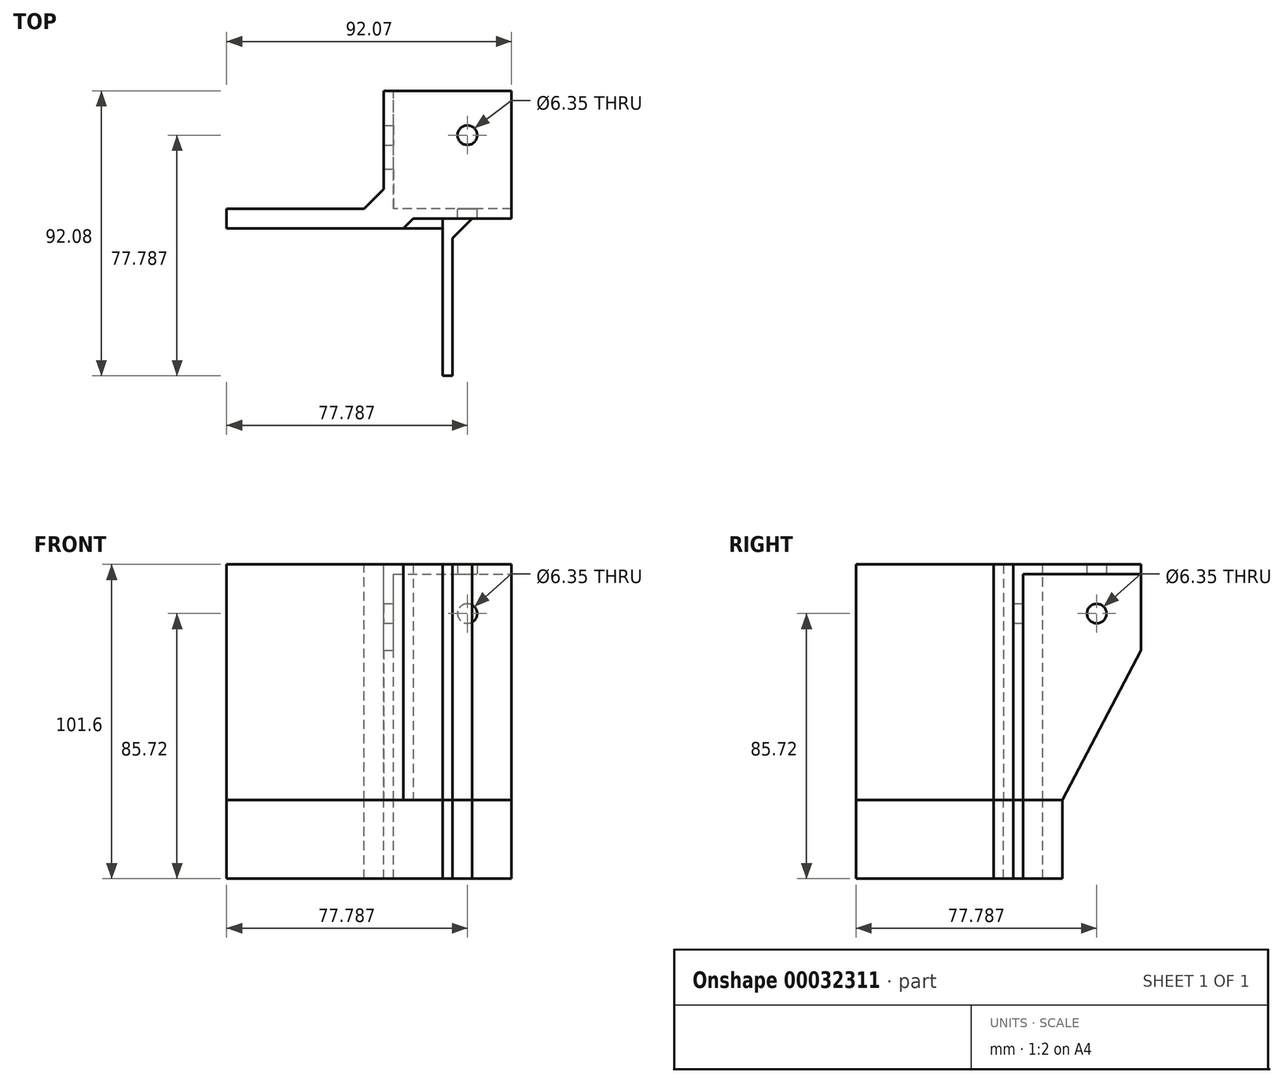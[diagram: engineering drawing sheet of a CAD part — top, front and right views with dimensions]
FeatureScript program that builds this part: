
annotation { "Feature Type Name" : "Feature", "Feature Type Description" : "" }
export const myFeature = defineFeature(function(context is Context, id is Id, definition is map)
    precondition{}
    {
        {
            var Q0;
            Q0=qCreatedBy(makeId("Top.planeOp"),FACE);
            var sketch = newSketch(context, id + "F0", { "sketchPlane" : qUnion([Q0])});
            skLineSegment(sketch, "E0.bottom", {"start": v(0, 0) * mm, "end": v(50.8, 0) * mm});
            skLineSegment(sketch, "E0.top", {"start": v(0, 50.8) * mm, "end": v(50.8, 50.8) * mm});
            skLineSegment(sketch, "E0.left", {"start": v(0, 0) * mm, "end": v(0, 50.8) * mm});
            skLineSegment(sketch, "E0.right", {"start": v(50.8, 0) * mm, "end": v(50.8, 50.8) * mm});
            skSolve(sketch);
        }
        {
            var Q0;
            Q0=makeQuery(id+"F0.imprint","IMPRINT",FACE,{"disambiguationData":[TD([[makeQuery(id+"F0.imprint","IMPRINT",EDGE,{"derivedFrom":sQuery(id+"F0.wireOp",EDGE,"E0.bottom")}),1.0]])]});
            extrude(context, id + "F1", {"entities" : qUnion([Q0]), "depth" : 3.17 * mm});
        }
        {
            var Q0;
            Q0=makeQuery(id+"F1.opExtrude","CAP_FACE",FACE,{"disambiguationData":[OSD([sQuery(id+"F0.wireOp",EDGE,"E0.bottom"),sQuery(id+"F0.wireOp",EDGE,"E0.top"),sQuery(id+"F0.wireOp",EDGE,"E0.left"),sQuery(id+"F0.wireOp",EDGE,"E0.right")])],"isStart":false});
            var sketch = newSketch(context, id + "F2", { "sketchPlane" : qUnion([Q0])});
            skLineSegment(sketch, "E1.bottom", {"start": v(50.8, 0) * mm, "end": v(-50.8, 0) * mm});
            skLineSegment(sketch, "E1.top", {"start": v(50.8, 3.18) * mm, "end": v(-50.8, 3.18) * mm});
            skLineSegment(sketch, "E1.left", {"start": v(50.8, 0) * mm, "end": v(50.8, 3.18) * mm});
            skLineSegment(sketch, "E1.right", {"start": v(-50.8, 0) * mm, "end": v(-50.8, 3.18) * mm});
            skSolve(sketch);
        }
        {
            var Q0;
            {var subQ5=sQuery(id+"F2.wireOp",EDGE,"E1.right");Q0=makeQuery(id+"F2.imprint","IMPRINT",FACE,{"disambiguationData":[TD([[makeQuery(id+"F2.imprint","IMPRINT",EDGE,{"derivedFrom":subQ5}),-1.0]])]});}
            var Q1;
            {var subQ5=sQuery(id+"F2.wireOp",EDGE,"E1.left");Q1=makeQuery(id+"F2.imprint","IMPRINT",FACE,{"disambiguationData":[TD([[makeQuery(id+"F2.imprint","IMPRINT",EDGE,{"derivedFrom":subQ5}),1.0]])]});}
            extrude(context, id + "F3", {"entities" : qUnion([Q0, Q1]), "operationType" : NewBodyOperationType.ADD, "depth" : 12.7 * mm, "hasSecondDirection" : true, "secondDirectionOppositeDirection" : true, "secondDirectionDepth" : 76.2 * mm});
        }
        {
            var Q0;
            Q0=makeQuery(id+"F1.opExtrude","CAP_FACE",FACE,{"disambiguationData":[OSD([sQuery(id+"F0.wireOp",EDGE,"E0.bottom"),sQuery(id+"F0.wireOp",EDGE,"E0.top"),sQuery(id+"F0.wireOp",EDGE,"E0.left"),sQuery(id+"F0.wireOp",EDGE,"E0.right")])],"isStart":false});
            var sketch = newSketch(context, id + "F4", { "sketchPlane" : qUnion([Q0])});
            skLineSegment(sketch, "E2.bottom", {"start": v(0, 50.8) * mm, "end": v(3.18, 50.8) * mm});
            skLineSegment(sketch, "E2.top", {"start": v(0, -50.8) * mm, "end": v(3.18, -50.8) * mm});
            skLineSegment(sketch, "E2.left", {"start": v(0, 50.8) * mm, "end": v(0, -50.8) * mm});
            skLineSegment(sketch, "E2.right", {"start": v(3.18, 50.8) * mm, "end": v(3.18, -50.8) * mm});
            skSolve(sketch);
        }
        {
            var Q0;
            Q0=qSketchRegion(id+"F4",true);
            extrude(context, id + "F5", {"entities" : qUnion([Q0]), "operationType" : NewBodyOperationType.ADD, "depth" : 12.7 * mm, "hasSecondDirection" : true, "secondDirectionOppositeDirection" : true, "secondDirectionDepth" : 76.2 * mm});
        }
        {
            var Q0;
            Q0=makeQuery(id+"F5.boolean.opBoolean","MERGE",FACE,{"derivedFrom":[makeQuery(id+"F3.opExtrude","CAP_FACE",FACE,{"disambiguationData":[OSD([sQuery(id+"F2.wireOp",EDGE,"E1.bottom"),sQuery(id+"F2.wireOp",EDGE,"E1.top"),sQuery(id+"F2.wireOp",EDGE,"E1.left"),sQuery(id+"F2.wireOp",EDGE,"E1.right")])],"isStart":false}),makeQuery(id+"F5.opExtrude","CAP_FACE",FACE,{"disambiguationData":[OSD([sQuery(id+"F4.wireOp",EDGE,"E2.bottom"),sQuery(id+"F4.wireOp",EDGE,"E2.top"),sQuery(id+"F4.wireOp",EDGE,"E2.left"),sQuery(id+"F4.wireOp",EDGE,"E2.right")])],"isStart":false})]});
            var sketch = newSketch(context, id + "F6", { "sketchPlane" : qUnion([Q0])});
            skLineSegment(sketch, "E3.0", {"start": v(3.18, 50.8) * mm, "end": v(3.18, 3.18) * mm});
            skLineSegment(sketch, "E3.1", {"start": v(0, 50.8) * mm, "end": v(3.18, 50.8) * mm});
            skLineSegment(sketch, "E3.2", {"start": v(0, 50.8) * mm, "end": v(0, 3.18) * mm});
            skLineSegment(sketch, "E3.3", {"start": v(50.8, 3.18) * mm, "end": v(3.18, 3.18) * mm});
            skLineSegment(sketch, "E3.4", {"start": v(50.8, 0) * mm, "end": v(3.18, 0) * mm});
            skLineSegment(sketch, "E3.5", {"start": v(50.8, 0) * mm, "end": v(50.8, 3.18) * mm});
            skLineSegment(sketch, "E4", {"start": v(3.18, 0) * mm, "end": v(0, 0) * mm});
            skLineSegment(sketch, "E5", {"start": v(0, 0) * mm, "end": v(0, 3.18) * mm});
            skSolve(sketch);
        }
        {
            var Q0;
            {var subQ0=sQuery(id+"F4.wireOp",EDGE,"E2.right");var subQ3=sQuery(id+"F0.wireOp",EDGE,"E0.top");Q0=makeQuery(id+"F5.boolean.opBoolean","SPLIT",FACE,{"disambiguationData":[TD([makeQuery(id+"F1.opExtrude","CAP_FACE",FACE,{"disambiguationData":[OSD([sQuery(id+"F0.wireOp",EDGE,"E0.bottom"),subQ3,sQuery(id+"F0.wireOp",EDGE,"E0.left"),sQuery(id+"F0.wireOp",EDGE,"E0.right")])],"isStart":false})])],"derivedFrom":makeQuery(id+"F5.opExtrude","SWEPT_FACE",FACE,{"disambiguationData":[OSD([subQ0])]})});}
            var sketch = newSketch(context, id + "F7", { "sketchPlane" : qUnion([Q0])});
            skLineSegment(sketch, "E6.0", {"start": v(50.8, 15.88) * mm, "end": v(50.8, 3.18) * mm});
            skLineSegment(sketch, "E6.1", {"start": v(3.18, 3.18) * mm, "end": v(50.8, 3.18) * mm});
            skLineSegment(sketch, "E6.2", {"start": v(50.8, 15.88) * mm, "end": v(3.18, 15.88) * mm});
            skLineSegment(sketch, "E6.3", {"start": v(3.18, 3.18) * mm, "end": v(3.18, 15.88) * mm});
            skSolve(sketch);
        }
        {
            var Q0;
            Q0=makeQuery(id+"F7.imprint","IMPRINT",FACE,{"disambiguationData":[TD([[makeQuery(id+"F7.imprint","IMPRINT",EDGE,{"derivedFrom":sQuery(id+"F7.wireOp",EDGE,"E6.0")}),-1.0]])]});
            extrude(context, id + "F8", {"entities" : qUnion([Q0]), "operationType" : NewBodyOperationType.REMOVE, "oppositeDirection" : true, "depth" : 25.4 * mm});
        }
        {
            var Q0;
            {var subQ0=sQuery(id+"F2.wireOp",EDGE,"E1.top");var subQ1=makeQuery(id+"F3.opExtrude","SWEPT_FACE",FACE,{"disambiguationData":[OSD([subQ0])]});var subQ11=sQuery(id+"F0.wireOp",EDGE,"E0.left");var subQ12=sQuery(id+"F0.wireOp",EDGE,"E0.right");Q0=makeQuery(id+"F8.boolean.opBoolean","MERGE",FACE,{"derivedFrom":[makeQuery(id+"F5.boolean.opBoolean","SPLIT",FACE,{"disambiguationData":[TD([makeQuery(id+"F1.opExtrude","SWEPT_FACE",FACE,{"disambiguationData":[OSD([subQ11])]})])],"derivedFrom":subQ1}),makeQuery(id+"F5.boolean.opBoolean","SPLIT",FACE,{"disambiguationData":[TD([makeQuery(id+"F1.opExtrude","CAP_FACE",FACE,{"disambiguationData":[OSD([sQuery(id+"F0.wireOp",EDGE,"E0.bottom"),sQuery(id+"F0.wireOp",EDGE,"E0.top"),subQ11,subQ12])],"isStart":false})])],"derivedFrom":subQ1}),makeQuery(id+"F8.opExtrude","SWEPT_FACE",FACE,{"disambiguationData":[OSD([sQuery(id+"F7.wireOp",EDGE,"E6.3")])]})]});}
            var sketch = newSketch(context, id + "F9", { "sketchPlane" : qUnion([Q0])});
            skLineSegment(sketch, "E7.0", {"start": v(-50.8, 15.88) * mm, "end": v(-3.18, 15.88) * mm});
            skLineSegment(sketch, "E7.1", {"start": v(-3.18, 3.18) * mm, "end": v(-50.8, 3.18) * mm});
            skLineSegment(sketch, "E7.2", {"start": v(-50.8, 15.88) * mm, "end": v(-50.8, 3.18) * mm});
            skLineSegment(sketch, "E8", {"start": v(-3.18, 15.88) * mm, "end": v(-3.18, 3.18) * mm});
            skPoint(sketch, "E9.orphan", {"position": v(0, 3.18) * mm});
            skSolve(sketch);
        }
        {
            var Q0;
            Q0=makeQuery(id+"F9.imprint","IMPRINT",FACE,{"disambiguationData":[TD([[makeQuery(id+"F9.imprint","IMPRINT",EDGE,{"derivedFrom":sQuery(id+"F9.wireOp",EDGE,"E7.0")}),-1.0]])]});
            extrude(context, id + "F10", {"entities" : qUnion([Q0]), "operationType" : NewBodyOperationType.REMOVE, "oppositeDirection" : true, "depth" : 25.4 * mm});
        }
        {
            var Q0;
            {var subQ0=sQuery(id+"F2.wireOp",EDGE,"E1.bottom");Q0=makeQuery(id+"F5.boolean.opBoolean","SPLIT",FACE,{"disambiguationData":[TD([makeQuery(id+"F1.opExtrude","SWEPT_FACE",FACE,{"disambiguationData":[OSD([sQuery(id+"F0.wireOp",EDGE,"E0.right")])]})])],"derivedFrom":makeQuery(id+"F3.boolean.opBoolean","MERGE",FACE,{"derivedFrom":[makeQuery(id+"F1.opExtrude","SWEPT_FACE",FACE,{"disambiguationData":[OSD([sQuery(id+"F0.wireOp",EDGE,"E0.bottom")])]}),makeQuery(id+"F3.opExtrude","SWEPT_FACE",FACE,{"disambiguationData":[OSD([subQ0])]})]})});}
            var sketch = newSketch(context, id + "F11", { "sketchPlane" : qUnion([Q0])});
            skLineSegment(sketch, "E10", {"start": v(3.18, -73.03) * mm, "end": v(41.28, -73.03) * mm, "construction": true});
            skLineSegment(sketch, "E11", {"start": v(50.8, 0) * mm, "end": v(50.8, -6.35) * mm, "construction": true});
            skLineSegment(sketch, "E12", {"start": v(41.28, -73.03) * mm, "end": v(50.8, -6.35) * mm});
            skLineSegment(sketch, "E13", {"start": v(50.8, -6.35) * mm, "end": v(50.8, -73.03) * mm});
            skLineSegment(sketch, "E14", {"start": v(50.8, -73.03) * mm, "end": v(41.28, -73.03) * mm});
            skSolve(sketch);
        }
        {
            var Q0;
            Q0=makeQuery(id+"F11.imprint","IMPRINT",FACE,{"disambiguationData":[TD([[makeQuery(id+"F11.imprint","IMPRINT",EDGE,{"derivedFrom":sQuery(id+"F11.wireOp",EDGE,"E12")}),-1.0]])]});
            extrude(context, id + "F12", {"entities" : qUnion([Q0]), "operationType" : NewBodyOperationType.REMOVE, "oppositeDirection" : true, "depth" : 25.4 * mm});
        }
        {
            var Q0;
            Q0=makeQuery(id+"F5.boolean.opBoolean","MERGE",FACE,{"derivedFrom":[makeQuery(id+"F1.opExtrude","SWEPT_FACE",FACE,{"disambiguationData":[OSD([sQuery(id+"F0.wireOp",EDGE,"E0.left")])]}),makeQuery(id+"F5.opExtrude","SWEPT_FACE",FACE,{"disambiguationData":[OSD([sQuery(id+"F4.wireOp",EDGE,"E2.left")])]})]});
            var sketch = newSketch(context, id + "F13", { "sketchPlane" : qUnion([Q0])});
            skLineSegment(sketch, "E15", {"start": v(-50.8, 3.18) * mm, "end": v(-50.8, -6.35) * mm, "construction": true});
            skLineSegment(sketch, "E16", {"start": v(-50.8, -6.35) * mm, "end": v(-15.88, -73.03) * mm});
            skLineSegment(sketch, "E17", {"start": v(-15.88, -73.03) * mm, "end": v(-3.18, -73.03) * mm, "construction": true});
            skLineSegment(sketch, "E18", {"start": v(-50.8, -6.35) * mm, "end": v(-50.8, -73.03) * mm});
            skLineSegment(sketch, "E19", {"start": v(-50.8, -73.03) * mm, "end": v(-15.88, -73.03) * mm});
            skSolve(sketch);
        }
        {
            var Q0;
            Q0=makeQuery(id+"F13.imprint","IMPRINT",FACE,{"disambiguationData":[TD([[makeQuery(id+"F13.imprint","IMPRINT",EDGE,{"derivedFrom":sQuery(id+"F13.wireOp",EDGE,"E16")}),-1.0]])]});
            extrude(context, id + "F14", {"entities" : qUnion([Q0]), "operationType" : NewBodyOperationType.REMOVE, "oppositeDirection" : true, "depth" : 25.4 * mm});
        }
        {
            var Q0;
            {var subQ0=sQuery(id+"F2.wireOp",EDGE,"E1.top");var subQ1=makeQuery(id+"F3.opExtrude","SWEPT_FACE",FACE,{"disambiguationData":[OSD([subQ0])]});var subQ11=sQuery(id+"F0.wireOp",EDGE,"E0.left");var subQ12=sQuery(id+"F0.wireOp",EDGE,"E0.right");Q0=makeQuery(id+"F8.boolean.opBoolean","MERGE",FACE,{"derivedFrom":[makeQuery(id+"F5.boolean.opBoolean","SPLIT",FACE,{"disambiguationData":[TD([makeQuery(id+"F1.opExtrude","SWEPT_FACE",FACE,{"disambiguationData":[OSD([subQ11])]})])],"derivedFrom":subQ1}),makeQuery(id+"F5.boolean.opBoolean","SPLIT",FACE,{"disambiguationData":[TD([makeQuery(id+"F1.opExtrude","CAP_FACE",FACE,{"disambiguationData":[OSD([sQuery(id+"F0.wireOp",EDGE,"E0.bottom"),sQuery(id+"F0.wireOp",EDGE,"E0.top"),subQ11,subQ12])],"isStart":false})])],"derivedFrom":subQ1}),makeQuery(id+"F8.opExtrude","SWEPT_FACE",FACE,{"disambiguationData":[OSD([sQuery(id+"F7.wireOp",EDGE,"E6.3")])]})]});}
            var sketch = newSketch(context, id + "F15", { "sketchPlane" : qUnion([Q0])});
            skLineSegment(sketch, "E20.bottom", {"start": v(-3.18, 15.88) * mm, "end": v(50.8, 15.88) * mm});
            skLineSegment(sketch, "E20.top", {"start": v(-3.18, 3.18) * mm, "end": v(50.8, 3.18) * mm});
            skLineSegment(sketch, "E20.left", {"start": v(-3.18, 15.88) * mm, "end": v(-3.18, 3.18) * mm});
            skLineSegment(sketch, "E20.right", {"start": v(50.8, 15.88) * mm, "end": v(50.8, 3.18) * mm});
            skSolve(sketch);
        }
        {
            var Q0;
            Q0=makeQuery(id+"F15.imprint","IMPRINT",FACE,{"disambiguationData":[TD([[makeQuery(id+"F15.imprint","IMPRINT",EDGE,{"derivedFrom":sQuery(id+"F15.wireOp",EDGE,"E20.bottom")}),-1.0]])]});
            extrude(context, id + "F16", {"entities" : qUnion([Q0]), "operationType" : NewBodyOperationType.REMOVE, "endBound" : BoundingType.THROUGH_ALL, "oppositeDirection" : true, "depth" : 25.4 * mm});
        }
        {
            var Q0;
            Q0=makeQuery(id+"F16.boolean.opBoolean","MERGE",FACE,{"derivedFrom":[makeQuery(id+"F10.boolean.opBoolean","MERGE",FACE,{"derivedFrom":[makeQuery(id+"F8.boolean.opBoolean","MERGE",FACE,{"derivedFrom":[makeQuery(id+"F1.opExtrude","CAP_FACE",FACE,{"disambiguationData":[OSD([sQuery(id+"F0.wireOp",EDGE,"E0.bottom"),sQuery(id+"F0.wireOp",EDGE,"E0.top"),sQuery(id+"F0.wireOp",EDGE,"E0.left"),sQuery(id+"F0.wireOp",EDGE,"E0.right")])],"isStart":false}),makeQuery(id+"F8.opExtrude","SWEPT_FACE",FACE,{"disambiguationData":[OSD([sQuery(id+"F7.wireOp",EDGE,"E6.1")])]})]}),makeQuery(id+"F10.opExtrude","SWEPT_FACE",FACE,{"disambiguationData":[OSD([sQuery(id+"F9.wireOp",EDGE,"E7.1")])]})]}),makeQuery(id+"F16.opExtrude","SWEPT_FACE",FACE,{"disambiguationData":[OSD([sQuery(id+"F15.wireOp",EDGE,"E20.top")])]})]});
            var sketch = newSketch(context, id + "F17", { "sketchPlane" : qUnion([Q0])});
            skLineSegment(sketch, "E21", {"start": v(3.18, 0) * mm, "end": v(3.18, -6.35) * mm});
            skLineSegment(sketch, "E22", {"start": v(3.18, -6.35) * mm, "end": v(9.53, 0) * mm});
            skLineSegment(sketch, "E23", {"start": v(9.53, 0) * mm, "end": v(3.18, 0) * mm});
            skLineSegment(sketch, "E24", {"start": v(0, 3.18) * mm, "end": v(0, 9.53) * mm});
            skLineSegment(sketch, "E25", {"start": v(0, 9.53) * mm, "end": v(-6.35, 3.18) * mm});
            skLineSegment(sketch, "E26", {"start": v(-6.35, 3.18) * mm, "end": v(0, 3.18) * mm});
            skSolve(sketch);
        }
        {
            var Q0;
            Q0=qSketchRegion(id+"F17",true);
            var Q1;
            Q1=makeQuery(id+"F5.boolean.opBoolean","MERGE",FACE,{"derivedFrom":[makeQuery(id+"F3.opExtrude","CAP_FACE",FACE,{"disambiguationData":[OSD([sQuery(id+"F2.wireOp",EDGE,"E1.bottom"),sQuery(id+"F2.wireOp",EDGE,"E1.top"),sQuery(id+"F2.wireOp",EDGE,"E1.left"),sQuery(id+"F2.wireOp",EDGE,"E1.right")])],"isStart":true}),makeQuery(id+"F5.opExtrude","CAP_FACE",FACE,{"disambiguationData":[OSD([sQuery(id+"F4.wireOp",EDGE,"E2.bottom"),sQuery(id+"F4.wireOp",EDGE,"E2.top"),sQuery(id+"F4.wireOp",EDGE,"E2.left"),sQuery(id+"F4.wireOp",EDGE,"E2.right")])],"isStart":true})]});
            extrude(context, id + "F18", {"entities" : qUnion([Q0]), "operationType" : NewBodyOperationType.ADD, "endBound" : BoundingType.UP_TO_SURFACE, "oppositeDirection" : true, "endBoundEntityFace" : qUnion([Q1]), "depth" : 25.4 * mm});
        }
        {
            var Q0;
            {var subQ0=sQuery(id+"F2.wireOp",EDGE,"E1.top");var subQ3=sQuery(id+"F0.wireOp",EDGE,"E0.right");Q0=makeQuery(id+"F5.boolean.opBoolean","SPLIT",FACE,{"disambiguationData":[TD([makeQuery(id+"F1.opExtrude","CAP_FACE",FACE,{"disambiguationData":[OSD([sQuery(id+"F0.wireOp",EDGE,"E0.bottom"),sQuery(id+"F0.wireOp",EDGE,"E0.top"),sQuery(id+"F0.wireOp",EDGE,"E0.left"),subQ3])],"isStart":true})])],"derivedFrom":makeQuery(id+"F3.opExtrude","SWEPT_FACE",FACE,{"disambiguationData":[OSD([subQ0])]})});}
            var sketch = newSketch(context, id + "F19", { "sketchPlane" : qUnion([Q0])});
            skLineSegment(sketch, "E27", {"start": v(-26.99, 0) * mm, "end": v(-26.99, -12.7) * mm, "construction": true});
            skPoint(sketch, "E27.endSnap0", {"position": v(-26.99, 0) * mm});
            skCircle(sketch, "E28", {"center": v(-26.99, -12.7) * mm, "radius": 3.18 * mm});
            skSolve(sketch);
        }
        {
            var Q0;
            Q0=qSketchRegion(id+"F19",true);
            extrude(context, id + "F20", {"entities" : qUnion([Q0]), "operationType" : NewBodyOperationType.REMOVE, "oppositeDirection" : true, "depth" : 25.4 * mm});
        }
        {
            var Q0;
            {var subQ0=sQuery(id+"F4.wireOp",EDGE,"E2.right");var subQ3=sQuery(id+"F0.wireOp",EDGE,"E0.top");Q0=makeQuery(id+"F5.boolean.opBoolean","SPLIT",FACE,{"disambiguationData":[TD([makeQuery(id+"F1.opExtrude","CAP_FACE",FACE,{"disambiguationData":[OSD([sQuery(id+"F0.wireOp",EDGE,"E0.bottom"),subQ3,sQuery(id+"F0.wireOp",EDGE,"E0.left"),sQuery(id+"F0.wireOp",EDGE,"E0.right")])],"isStart":true})])],"derivedFrom":makeQuery(id+"F5.opExtrude","SWEPT_FACE",FACE,{"disambiguationData":[OSD([subQ0])]})});}
            var sketch = newSketch(context, id + "F21", { "sketchPlane" : qUnion([Q0])});
            skLineSegment(sketch, "E29", {"start": v(26.99, 0) * mm, "end": v(26.99, -12.7) * mm, "construction": true});
            skPoint(sketch, "E29.endSnap0", {"position": v(26.99, 0) * mm});
            skCircle(sketch, "E30", {"center": v(26.99, -12.7) * mm, "radius": 3.18 * mm});
            skSolve(sketch);
        }
        {
            var Q0;
            Q0=makeQuery(id+"F21.imprint","IMPRINT",FACE,{"disambiguationData":[TD([[makeQuery(id+"F21.imprint","IMPRINT",EDGE,{"derivedFrom":sQuery(id+"F21.wireOp",EDGE,"E30")}),1.0]])]});
            extrude(context, id + "F22", {"entities" : qUnion([Q0]), "operationType" : NewBodyOperationType.REMOVE, "oppositeDirection" : true, "depth" : 25.4 * mm});
        }
        {
            var Q0;
            Q0=makeQuery(id+"F1.opExtrude","CAP_FACE",FACE,{"disambiguationData":[OSD([sQuery(id+"F0.wireOp",EDGE,"E0.bottom"),sQuery(id+"F0.wireOp",EDGE,"E0.top"),sQuery(id+"F0.wireOp",EDGE,"E0.left"),sQuery(id+"F0.wireOp",EDGE,"E0.right")])],"isStart":true});
            var sketch = newSketch(context, id + "F23", { "sketchPlane" : qUnion([Q0])});
            skLineSegment(sketch, "E31", {"start": v(3.18, -3.18) * mm, "end": v(50.8, -50.8) * mm, "construction": true});
            skLineSegment(sketch, "E32", {"start": v(50.8, -50.8) * mm, "end": v(50.8, -3.18) * mm, "construction": true});
            skLineSegment(sketch, "E33", {"start": v(50.8, -3.18) * mm, "end": v(3.17, -50.8) * mm, "construction": true});
            skCircle(sketch, "E34", {"center": v(26.99, -26.99) * mm, "radius": 3.18 * mm});
            skPoint(sketch, "E34.centerSnap0", {"position": v(26.99, -26.99) * mm});
            skSolve(sketch);
        }
        {
            var Q0;
            Q0=makeQuery(id+"F23.imprint","IMPRINT",FACE,{"disambiguationData":[TD([[makeQuery(id+"F23.imprint","IMPRINT",EDGE,{"derivedFrom":sQuery(id+"F23.wireOp",EDGE,"E34")}),1.0]])]});
            var Q1;
            Q1=sQuery(id+"F23.wireOp",EDGE,"E34");
            extrude(context, id + "F24", {"entities" : qUnion([Q0]), "operationType" : NewBodyOperationType.REMOVE, "surfaceEntities" : qUnion([Q1]), "oppositeDirection" : true, "depth" : 25.4 * mm});
        }
        {
            var Q0;
            Q0=makeQuery(id+"F18.boolean.opBoolean","MERGE",FACE,{"derivedFrom":[makeQuery(id+"F16.boolean.opBoolean","MERGE",FACE,{"derivedFrom":[makeQuery(id+"F10.boolean.opBoolean","MERGE",FACE,{"derivedFrom":[makeQuery(id+"F8.boolean.opBoolean","MERGE",FACE,{"derivedFrom":[makeQuery(id+"F1.opExtrude","CAP_FACE",FACE,{"disambiguationData":[OSD([sQuery(id+"F0.wireOp",EDGE,"E0.bottom"),sQuery(id+"F0.wireOp",EDGE,"E0.top"),sQuery(id+"F0.wireOp",EDGE,"E0.left"),sQuery(id+"F0.wireOp",EDGE,"E0.right")])],"isStart":false}),makeQuery(id+"F8.opExtrude","SWEPT_FACE",FACE,{"disambiguationData":[OSD([sQuery(id+"F7.wireOp",EDGE,"E6.1")])]})]}),makeQuery(id+"F10.opExtrude","SWEPT_FACE",FACE,{"disambiguationData":[OSD([sQuery(id+"F9.wireOp",EDGE,"E7.1")])]})]}),makeQuery(id+"F16.opExtrude","SWEPT_FACE",FACE,{"disambiguationData":[OSD([sQuery(id+"F15.wireOp",EDGE,"E20.top")])]})]}),makeQuery(id+"F18.opExtrude","CAP_FACE",FACE,{"disambiguationData":[OSD([sQuery(id+"F17.wireOp",EDGE,"E21"),sQuery(id+"F17.wireOp",EDGE,"E22"),sQuery(id+"F17.wireOp",EDGE,"E23")])],"isStart":true}),makeQuery(id+"F18.opExtrude","CAP_FACE",FACE,{"disambiguationData":[OSD([sQuery(id+"F17.wireOp",EDGE,"E24"),sQuery(id+"F17.wireOp",EDGE,"E25"),sQuery(id+"F17.wireOp",EDGE,"E26")])],"isStart":true})]});
            var sketch = newSketch(context, id + "F25", { "sketchPlane" : qUnion([Q0])});
            skLineSegment(sketch, "E35.bottom", {"start": v(50.8, 0) * mm, "end": v(41.28, 0) * mm});
            skLineSegment(sketch, "E35.top", {"start": v(50.8, 50.8) * mm, "end": v(41.27, 50.8) * mm});
            skLineSegment(sketch, "E35.left", {"start": v(50.8, 0) * mm, "end": v(50.8, 50.8) * mm});
            skLineSegment(sketch, "E35.right", {"start": v(41.28, 0) * mm, "end": v(41.27, 41.28) * mm});
            skLineSegment(sketch, "E36.bottom", {"start": v(41.27, 50.8) * mm, "end": v(0, 50.8) * mm});
            skLineSegment(sketch, "E36.top", {"start": v(41.27, 41.28) * mm, "end": v(0, 41.28) * mm});
            skLineSegment(sketch, "E36.right", {"start": v(0, 50.8) * mm, "end": v(0, 41.28) * mm});
            skSolve(sketch);
        }
        {
            var Q0;
            Q0=makeQuery(id+"F25.imprint","IMPRINT",FACE,{"disambiguationData":[TD([[makeQuery(id+"F25.imprint","IMPRINT",EDGE,{"derivedFrom":sQuery(id+"F25.wireOp",EDGE,"E35.bottom")}),1.0]])]});
            extrude(context, id + "F26", {"entities" : qUnion([Q0]), "operationType" : NewBodyOperationType.REMOVE, "endBound" : BoundingType.THROUGH_ALL, "oppositeDirection" : true, "depth" : 25.4 * mm});
        }
        {
            var Q0;
            {var subQ0=sQuery(id+"F2.wireOp",EDGE,"E1.bottom");var subQ5=sQuery(id+"F2.wireOp",EDGE,"E1.right");Q0=makeQuery(id+"F5.boolean.opBoolean","SPLIT",FACE,{"disambiguationData":[TD([makeQuery(id+"F3.opExtrude","SWEPT_FACE",FACE,{"disambiguationData":[OSD([subQ5])]})])],"derivedFrom":makeQuery(id+"F3.boolean.opBoolean","MERGE",FACE,{"derivedFrom":[makeQuery(id+"F1.opExtrude","SWEPT_FACE",FACE,{"disambiguationData":[OSD([sQuery(id+"F0.wireOp",EDGE,"E0.bottom")])]}),makeQuery(id+"F3.opExtrude","SWEPT_FACE",FACE,{"disambiguationData":[OSD([subQ0])]})]})});}
            extrude(context, id + "F27", {"entities" : qUnion([Q0]), "operationType" : NewBodyOperationType.ADD, "depth" : 3.17 * mm});
        }
        {
            var Q0;
            {var subQ0=sQuery(id+"F0.wireOp",EDGE,"E0.bottom");var subQ1=sQuery(id+"F15.wireOp",EDGE,"E20.top");Q0=makeQuery(id+"F27.boolean.opBoolean","MERGE",FACE,{"derivedFrom":[makeQuery(id+"F18.boolean.opBoolean","MERGE",FACE,{"derivedFrom":[makeQuery(id+"F16.boolean.opBoolean","MERGE",FACE,{"derivedFrom":[makeQuery(id+"F10.boolean.opBoolean","MERGE",FACE,{"derivedFrom":[makeQuery(id+"F8.boolean.opBoolean","MERGE",FACE,{"derivedFrom":[makeQuery(id+"F1.opExtrude","CAP_FACE",FACE,{"disambiguationData":[OSD([subQ0,sQuery(id+"F0.wireOp",EDGE,"E0.top"),sQuery(id+"F0.wireOp",EDGE,"E0.left"),sQuery(id+"F0.wireOp",EDGE,"E0.right")])],"isStart":false}),makeQuery(id+"F8.opExtrude","SWEPT_FACE",FACE,{"disambiguationData":[OSD([sQuery(id+"F7.wireOp",EDGE,"E6.1")])]})]}),makeQuery(id+"F10.opExtrude","SWEPT_FACE",FACE,{"disambiguationData":[OSD([sQuery(id+"F9.wireOp",EDGE,"E7.1")])]})]}),makeQuery(id+"F16.opExtrude","SWEPT_FACE",FACE,{"disambiguationData":[OSD([subQ1])]})]}),makeQuery(id+"F18.opExtrude","CAP_FACE",FACE,{"disambiguationData":[OSD([sQuery(id+"F17.wireOp",EDGE,"E21"),sQuery(id+"F17.wireOp",EDGE,"E22"),sQuery(id+"F17.wireOp",EDGE,"E23")])],"isStart":true}),makeQuery(id+"F18.opExtrude","CAP_FACE",FACE,{"disambiguationData":[OSD([sQuery(id+"F17.wireOp",EDGE,"E24"),sQuery(id+"F17.wireOp",EDGE,"E25"),sQuery(id+"F17.wireOp",EDGE,"E26")])],"isStart":true})]}),makeQuery(id+"F27.opExtrude","SWEPT_FACE",FACE,{"disambiguationData":[OSD([subQ0,sQuery(id+"F2.wireOp",EDGE,"E1.bottom"),subQ1])]})]});}
            var sketch = newSketch(context, id + "F28", { "sketchPlane" : qUnion([Q0])});
            skLineSegment(sketch, "E37", {"start": v(3.18, -12.1) * mm, "end": v(22.23, -12.1) * mm, "construction": true});
            skPoint(sketch, "E38.oppositeSnap0", {"position": v(1.59, -50.8) * mm});
            skLineSegment(sketch, "E38.bottom", {"start": v(22.23, 0) * mm, "end": v(19.05, 0) * mm});
            skLineSegment(sketch, "E38.top", {"start": v(22.23, -50.8) * mm, "end": v(19.05, -50.8) * mm});
            skLineSegment(sketch, "E38.left", {"start": v(22.23, -6.35) * mm, "end": v(22.23, -50.8) * mm});
            skLineSegment(sketch, "E38.right", {"start": v(19.05, 0) * mm, "end": v(19.05, -50.8) * mm});
            skLineSegment(sketch, "E39", {"start": v(22.23, 0) * mm, "end": v(28.57, 0) * mm});
            skLineSegment(sketch, "E40", {"start": v(28.57, 0) * mm, "end": v(22.23, -6.35) * mm});
            skSolve(sketch);
        }
        {
            var Q0;
            Q0=makeQuery(id+"F28.imprint","IMPRINT",FACE,{"disambiguationData":[TD([[makeQuery(id+"F28.imprint","IMPRINT",EDGE,{"derivedFrom":sQuery(id+"F28.wireOp",EDGE,"E38.bottom")}),-1.0]])]});
            var Q1;
            {var subQ0=sQuery(id+"F2.wireOp",EDGE,"E1.bottom");Q1=makeQuery(id+"F27.boolean.opBoolean","MERGE",FACE,{"derivedFrom":[makeQuery(id+"F18.boolean.opBoolean","MERGE",FACE,{"derivedFrom":[makeQuery(id+"F5.boolean.opBoolean","MERGE",FACE,{"derivedFrom":[makeQuery(id+"F3.opExtrude","CAP_FACE",FACE,{"disambiguationData":[OSD([subQ0,sQuery(id+"F2.wireOp",EDGE,"E1.top"),sQuery(id+"F2.wireOp",EDGE,"E1.left"),sQuery(id+"F2.wireOp",EDGE,"E1.right")])],"isStart":true}),makeQuery(id+"F5.opExtrude","CAP_FACE",FACE,{"disambiguationData":[OSD([sQuery(id+"F4.wireOp",EDGE,"E2.bottom"),sQuery(id+"F4.wireOp",EDGE,"E2.top"),sQuery(id+"F4.wireOp",EDGE,"E2.left"),sQuery(id+"F4.wireOp",EDGE,"E2.right")])],"isStart":true})]}),makeQuery(id+"F18.opExtrude","CAP_FACE",FACE,{"disambiguationData":[OSD([sQuery(id+"F17.wireOp",EDGE,"E21"),sQuery(id+"F17.wireOp",EDGE,"E22"),sQuery(id+"F17.wireOp",EDGE,"E23")])],"isStart":false}),makeQuery(id+"F18.opExtrude","CAP_FACE",FACE,{"disambiguationData":[OSD([sQuery(id+"F17.wireOp",EDGE,"E24"),sQuery(id+"F17.wireOp",EDGE,"E25"),sQuery(id+"F17.wireOp",EDGE,"E26")])],"isStart":false})]}),makeQuery(id+"F27.opExtrude","SWEPT_FACE",FACE,{"disambiguationData":[OSD([subQ0])]})]});}
            extrude(context, id + "F29", {"entities" : qUnion([Q0]), "endBound" : BoundingType.UP_TO_SURFACE, "oppositeDirection" : true, "endBoundEntityFace" : qUnion([Q1]), "depth" : 25.4 * mm});
        }
        {
            var Q0;
            {var subQ0=sQuery(id+"F0.wireOp",EDGE,"E0.bottom");var subQ1=sQuery(id+"F15.wireOp",EDGE,"E20.top");Q0=makeQuery(id+"F27.boolean.opBoolean","MERGE",FACE,{"derivedFrom":[makeQuery(id+"F18.boolean.opBoolean","MERGE",FACE,{"derivedFrom":[makeQuery(id+"F16.boolean.opBoolean","MERGE",FACE,{"derivedFrom":[makeQuery(id+"F10.boolean.opBoolean","MERGE",FACE,{"derivedFrom":[makeQuery(id+"F8.boolean.opBoolean","MERGE",FACE,{"derivedFrom":[makeQuery(id+"F1.opExtrude","CAP_FACE",FACE,{"disambiguationData":[OSD([subQ0,sQuery(id+"F0.wireOp",EDGE,"E0.top"),sQuery(id+"F0.wireOp",EDGE,"E0.left"),sQuery(id+"F0.wireOp",EDGE,"E0.right")])],"isStart":false}),makeQuery(id+"F8.opExtrude","SWEPT_FACE",FACE,{"disambiguationData":[OSD([sQuery(id+"F7.wireOp",EDGE,"E6.1")])]})]}),makeQuery(id+"F10.opExtrude","SWEPT_FACE",FACE,{"disambiguationData":[OSD([sQuery(id+"F9.wireOp",EDGE,"E7.1")])]})]}),makeQuery(id+"F16.opExtrude","SWEPT_FACE",FACE,{"disambiguationData":[OSD([subQ1])]})]}),makeQuery(id+"F18.opExtrude","CAP_FACE",FACE,{"disambiguationData":[OSD([sQuery(id+"F17.wireOp",EDGE,"E21"),sQuery(id+"F17.wireOp",EDGE,"E22"),sQuery(id+"F17.wireOp",EDGE,"E23")])],"isStart":true}),makeQuery(id+"F18.opExtrude","CAP_FACE",FACE,{"disambiguationData":[OSD([sQuery(id+"F17.wireOp",EDGE,"E24"),sQuery(id+"F17.wireOp",EDGE,"E25"),sQuery(id+"F17.wireOp",EDGE,"E26")])],"isStart":true})]}),makeQuery(id+"F27.opExtrude","SWEPT_FACE",FACE,{"disambiguationData":[OSD([subQ0,sQuery(id+"F2.wireOp",EDGE,"E1.bottom"),subQ1])]})]});}
            var sketch = newSketch(context, id + "F30", { "sketchPlane" : qUnion([Q0])});
            skLineSegment(sketch, "E41.0", {"start": v(3.18, -50.8) * mm, "end": v(3.18, -6.35) * mm});
            skLineSegment(sketch, "E41.1", {"start": v(3.17, -6.35) * mm, "end": v(6.35, -3.18) * mm});
            skLineSegment(sketch, "E41.2", {"start": v(0, -3.18) * mm, "end": v(0, -50.8) * mm});
            skLineSegment(sketch, "E41.3", {"start": v(0, -50.8) * mm, "end": v(3.18, -50.8) * mm});
            skLineSegment(sketch, "E42", {"start": v(0, -3.18) * mm, "end": v(6.35, -3.18) * mm});
            skPoint(sketch, "E43.orphan", {"position": v(9.53, 0) * mm});
            skSolve(sketch);
        }
        {
            var Q0;
            Q0=makeQuery(id+"F30.imprint","IMPRINT",FACE,{"disambiguationData":[TD([[makeQuery(id+"F30.imprint","IMPRINT",EDGE,{"derivedFrom":sQuery(id+"F30.wireOp",EDGE,"E41.0")}),1.0]])]});
            extrude(context, id + "F31", {"entities" : qUnion([Q0]), "operationType" : NewBodyOperationType.REMOVE, "endBound" : BoundingType.THROUGH_ALL, "oppositeDirection" : true, "depth" : 25.4 * mm});
        }
        {
            var Q0;
            Q0=makeQuery(id+"F29.opExtrude","SWEPT_FACE",FACE,{"disambiguationData":[OSD([sQuery(id+"F28.wireOp",EDGE,"E38.right")])]});
            var sketch = newSketch(context, id + "F32", { "sketchPlane" : qUnion([Q0])});
            skLineSegment(sketch, "E44.0", {"start": v(3.18, -73.02) * mm, "end": v(3.18, 3.18) * mm});
            skLineSegment(sketch, "E44.1", {"start": v(3.18, 3.18) * mm, "end": v(0, 3.18) * mm});
            skLineSegment(sketch, "E44.2", {"start": v(0, -73.02) * mm, "end": v(0, 3.17) * mm});
            skLineSegment(sketch, "E44.3", {"start": v(0, -73.02) * mm, "end": v(3.18, -73.02) * mm});
            skSolve(sketch);
        }
        {
            var Q0;
            Q0=qSketchRegion(id+"F32",true);
            extrude(context, id + "F33", {"entities" : qUnion([Q0]), "endBound" : BoundingType.UP_TO_NEXT, "depth" : 25.4 * mm});
        }
        {
            var Q0;
            {var subQ0=sQuery(id+"F2.wireOp",EDGE,"E1.bottom");Q0=makeQuery(id+"F27.boolean.opBoolean","MERGE",FACE,{"derivedFrom":[makeQuery(id+"F18.boolean.opBoolean","MERGE",FACE,{"derivedFrom":[makeQuery(id+"F5.boolean.opBoolean","MERGE",FACE,{"derivedFrom":[makeQuery(id+"F3.opExtrude","CAP_FACE",FACE,{"disambiguationData":[OSD([subQ0,sQuery(id+"F2.wireOp",EDGE,"E1.top"),sQuery(id+"F2.wireOp",EDGE,"E1.left"),sQuery(id+"F2.wireOp",EDGE,"E1.right")])],"isStart":true}),makeQuery(id+"F5.opExtrude","CAP_FACE",FACE,{"disambiguationData":[OSD([sQuery(id+"F4.wireOp",EDGE,"E2.bottom"),sQuery(id+"F4.wireOp",EDGE,"E2.top"),sQuery(id+"F4.wireOp",EDGE,"E2.left"),sQuery(id+"F4.wireOp",EDGE,"E2.right")])],"isStart":true})]}),makeQuery(id+"F18.opExtrude","CAP_FACE",FACE,{"disambiguationData":[OSD([sQuery(id+"F17.wireOp",EDGE,"E21"),sQuery(id+"F17.wireOp",EDGE,"E22"),sQuery(id+"F17.wireOp",EDGE,"E23")])],"isStart":false}),makeQuery(id+"F18.opExtrude","CAP_FACE",FACE,{"disambiguationData":[OSD([sQuery(id+"F17.wireOp",EDGE,"E24"),sQuery(id+"F17.wireOp",EDGE,"E25"),sQuery(id+"F17.wireOp",EDGE,"E26")])],"isStart":false})]}),makeQuery(id+"F27.opExtrude","SWEPT_FACE",FACE,{"disambiguationData":[OSD([subQ0])]})]});}
            var sketch = newSketch(context, id + "F34", { "sketchPlane" : qUnion([Q0])});
            skLineSegment(sketch, "E45.0", {"start": v(6.35, 3.18) * mm, "end": v(-50.8, 3.18) * mm});
            skLineSegment(sketch, "E45.1", {"start": v(-50.8, 3.18) * mm, "end": v(-50.8, -3.18) * mm});
            skLineSegment(sketch, "E45.2", {"start": v(-6.35, -3.18) * mm, "end": v(-50.8, -3.18) * mm});
            skLineSegment(sketch, "E45.3", {"start": v(-6.35, -3.18) * mm, "end": v(0, -9.53) * mm});
            skLineSegment(sketch, "E45.4", {"start": v(0, -15.88) * mm, "end": v(0, -9.53) * mm});
            skLineSegment(sketch, "E45.5", {"start": v(3.18, -15.88) * mm, "end": v(0, -15.88) * mm});
            skLineSegment(sketch, "E45.6", {"start": v(3.18, -15.88) * mm, "end": v(3.18, -3.18) * mm});
            skLineSegment(sketch, "E45.7", {"start": v(41.28, -3.18) * mm, "end": v(3.18, -3.18) * mm});
            skLineSegment(sketch, "E45.8", {"start": v(41.28, -3.18) * mm, "end": v(41.28, 0) * mm});
            skLineSegment(sketch, "E45.9", {"start": v(41.27, 0) * mm, "end": v(28.57, 0) * mm});
            skLineSegment(sketch, "E45.10", {"start": v(22.23, 6.35) * mm, "end": v(28.57, 0) * mm});
            skLineSegment(sketch, "E45.11", {"start": v(22.23, 50.8) * mm, "end": v(22.23, 6.35) * mm});
            skLineSegment(sketch, "E45.12", {"start": v(19.05, 50.8) * mm, "end": v(19.05, 3.18) * mm});
            skLineSegment(sketch, "E45.13", {"start": v(19.05, 50.8) * mm, "end": v(22.23, 50.8) * mm});
            skLineSegment(sketch, "E45.14", {"start": v(6.35, 3.18) * mm, "end": v(19.05, 3.18) * mm});
            skPoint(sketch, "E46.orphan", {"position": v(9.53, 0) * mm});
            skPoint(sketch, "E47.orphan", {"position": v(19.05, 0) * mm});
            skSolve(sketch);
        }
        {
            var Q0;
            Q0=qSketchRegion(id+"F34",true);
            extrude(context, id + "F35", {"entities" : qUnion([Q0]), "depth" : 25.4 * mm});
        }
    });
